# Revit family: ХЦ_Eng
name_source: partatom
category: Duct Fittings
units: mm (PartAtom-declared; Revit-internal decimal feet)

## family parameters
Always vertical = No
Cut with Voids When Loaded = No
Part Type = Union
Round Connector Dimension = Use Diameter
Shared = No
Work Plane-Based = No

## types (7) — shared parameters
00_20_Manufacturer = Vents
00_20_Name = Clamp
Length = 60 mm  [stored 0.19685 ft]
Load Classification = HVAC
Maintenance zone material = <By Category>
Manufacturer = Vents
URL = https://ventilation-system.com
zero-valued in all types: Default Elevation

## per-type parameters (varying)
| type | 00_20_Type | Casing Material | Diameter | Dn | Dy | H | Height | Rn | Ry | Weight | Width | h | h1 |
| CZ 100 | CZ 100 | Steel, galvanized | 100 mm  [stored 0.328084 ft] | 102 mm | 100 mm  [stored 0.328084 ft] | 172 mm  [stored 0.564304 ft] | 172 mm  [stored 0.564304 ft] | 51 mm | 50 mm  [stored 0.164042 ft] | 0.21 kg | 102 mm | 86 mm  [stored 0.282152 ft] | 71 mm  [stored 0.23294 ft] |
| CZ 315 | CZ 100 | Металл, окрашенный, синий, матовый RAL 5007 | 315 mm | 317 mm | 315 mm | 380 mm | 380 mm | 159 mm | 158 mm | 0.65 kg | 317 mm | 190 mm | 175 mm  [stored 0.574147 ft] |
| CZ 125 | CZ 125 | Металл, окрашенный, синий, матовый RAL 5007 | 125 mm  [stored 0.410105 ft] | 127 mm | 125 mm  [stored 0.410105 ft] | 198 mm  [stored 0.649606 ft] | 198 mm  [stored 0.649606 ft] | 64 mm | 63 mm | 0.23 kg | 127 mm | 99 mm  [stored 0.324803 ft] | 84 mm  [stored 0.275591 ft] |
| CZ 150 | CZ 150 | Металл, окрашенный, синий, матовый RAL 5007 | 150 mm | 152 mm  [stored 0.498688 ft] | 150 mm | 224 mm  [stored 0.734908 ft] | 224 mm  [stored 0.734908 ft] | 76 mm  [stored 0.249344 ft] | 75 mm | 0.30 kg | 152 mm  [stored 0.498688 ft] | 112 mm  [stored 0.367454 ft] | 97 mm  [stored 0.318241 ft] |
| CZ 160 | CZ 160 | Металл, окрашенный, синий, матовый RAL 5007 | 160 mm  [stored 0.524934 ft] | 162 mm  [stored 0.531496 ft] | 160 mm  [stored 0.524934 ft] | 232 mm | 232 mm | 81 mm  [stored 0.265748 ft] | 80 mm  [stored 0.262467 ft] | 0.36 kg | 162 mm  [stored 0.531496 ft] | 116 mm  [stored 0.380577 ft] | 101 mm  [stored 0.331365 ft] |
| CZ 200 | CZ 200 | Металл, окрашенный, синий, матовый RAL 5007 | 200 mm  [stored 0.656168 ft] | 202 mm  [stored 0.66273 ft] | 200 mm  [stored 0.656168 ft] | 274 mm | 274 mm | 101 mm  [stored 0.331365 ft] | 100 mm  [stored 0.328084 ft] | 0.42 kg | 202 mm  [stored 0.66273 ft] | 137 mm  [stored 0.449475 ft] | 122 mm  [stored 0.400262 ft] |
| CZ 250 | CZ 250 | Металл, окрашенный, синий, матовый RAL 5007 | 250 mm | 252 mm | 250 mm | 326 mm | 326 mm | 126 mm  [stored 0.413386 ft] | 125 mm  [stored 0.410105 ft] | 0.55 kg | 252 mm | 163 mm  [stored 0.534777 ft] | 148 mm  [stored 0.485564 ft] |

note: [stored X ft] marks values corroborated as IEEE doubles in the binary element streams (Revit-internal decimal feet)
